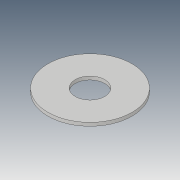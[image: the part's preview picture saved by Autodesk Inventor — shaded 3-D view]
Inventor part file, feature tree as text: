
AUTODESK INVENTOR PART (.ipt)
format: ipt  version: 2019 (Build 230136000, 136)  size: 79,360 bytes
history: native  units: mm
features: extrude x1, sketch x1
ambient origin geometry x8: Origin, YZ Plane, XZ Plane, XY Plane, X Axis, Y Axis, Z Axis, Center Point
bodies: Solid1 (feature_tree)
feature tree (2):
  extrude  "Extrusion1"  Depth=10.0mm
  sketch  "Sketch1"  dims[d0=3.5mm d1=10.0mm d2=0.4mm d3=0.0mm]
